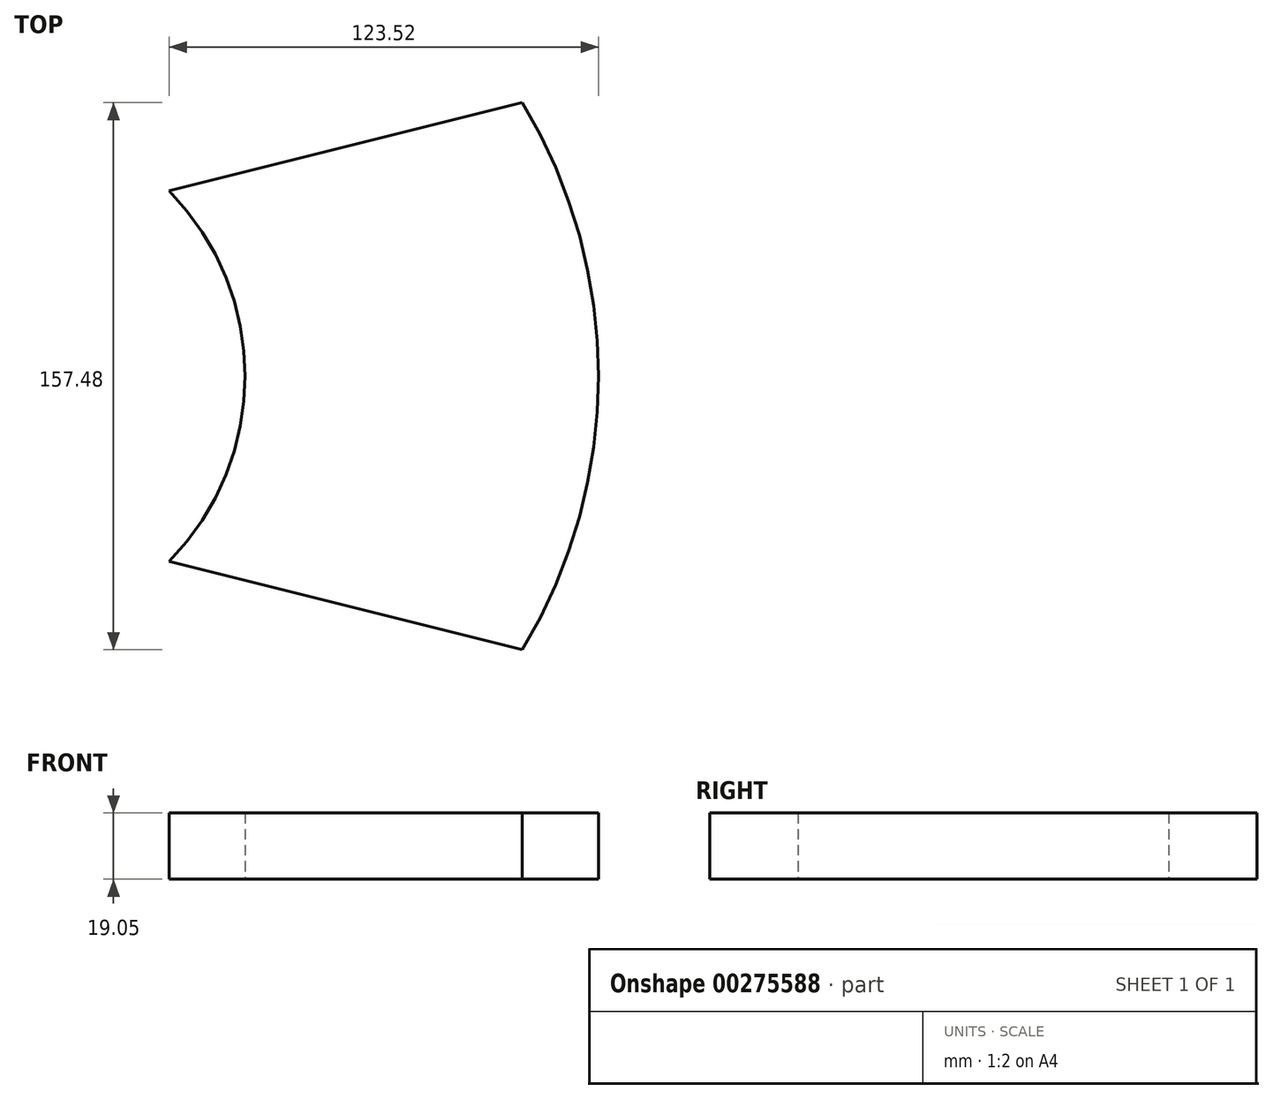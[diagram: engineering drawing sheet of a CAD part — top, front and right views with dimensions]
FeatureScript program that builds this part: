
annotation { "Feature Type Name" : "Feature", "Feature Type Description" : "" }
export const myFeature = defineFeature(function(context is Context, id is Id, definition is map)
    precondition{}
    {
        {
            var Q0;
            Q0=qCreatedBy(makeId("Top.planeOp"),FACE);
            var sketch = newSketch(context, id + "F0", { "sketchPlane" : qUnion([Q0])});
            skLineSegment(sketch, "E0", {"start": v(4.84, 0) * mm, "end": v(-47.06, 0) * mm});
            skLineSegment(sketch, "E1", {"start": v(-47.06, 0) * mm, "end": v(54.54, 0) * mm});
            skLineSegment(sketch, "E2", {"start": v(-47.06, 0) * mm, "end": v(-47.06, 81.28) * mm});
            skLineSegment(sketch, "E3", {"start": v(54.54, 0) * mm, "end": v(54.54, 106.68) * mm});
            skLineSegment(sketch, "E4", {"start": v(54.54, -50.8) * mm, "end": v(54.54, 0) * mm});
            skArc(sketch, "E5", {"start": v(54.54, -50.8) * mm, "mid": v(76.46, 27.94) * mm, "end": v(54.54, 106.68) * mm});
            skLineSegment(sketch, "E6", {"start": v(-47.06, 81.28) * mm, "end": v(54.54, 106.68) * mm});
            skLineSegment(sketch, "E7", {"start": v(-47.06, 0) * mm, "end": v(54.54, -50.8) * mm});
            skLineSegment(sketch, "E8", {"start": v(-47.06, 0) * mm, "end": v(-47.06, -25.4) * mm});
            skLineSegment(sketch, "E9", {"start": v(-47.06, -25.4) * mm, "end": v(54.54, -50.8) * mm});
            skArc(sketch, "E10", {"start": v(-47.06, -25.4) * mm, "mid": v(-25.28, 27.94) * mm, "end": v(-47.06, 81.28) * mm});
            skSolve(sketch);
        }
        {
            var Q0;
            {var subQ4=sQuery(id+"F0.wireOp",EDGE,"E3");Q0=makeQuery(id+"F0.imprint","IMPRINT",FACE,{"disambiguationData":[TD([[makeQuery(id+"F0.imprint","IMPRINT",EDGE,{"derivedFrom":subQ4}),1.0]])]});}
            var Q1;
            {var subQ1=sQuery(id+"F0.wireOp",EDGE,"E4");Q1=makeQuery(id+"F0.imprint","IMPRINT",FACE,{"disambiguationData":[TD([[makeQuery(id+"F0.imprint","IMPRINT",EDGE,{"derivedFrom":subQ1}),1.0]])]});}
            var Q2;
            {var subQ0=sQuery(id+"F0.wireOp",EDGE,"E9");Q2=makeQuery(id+"F0.imprint","IMPRINT",FACE,{"disambiguationData":[TD([[makeQuery(id+"F0.imprint","IMPRINT",EDGE,{"derivedFrom":subQ0}),1.0]])]});}
            var Q3;
            Q3=makeQuery(id+"F0.imprint","IMPRINT",FACE,{"disambiguationData":[TD([[makeQuery(id+"F0.imprint","IMPRINT",EDGE,{"derivedFrom":sQuery(id+"F0.wireOp",EDGE,"E3")}),-1.0]])]});
            extrude(context, id + "F1", {"entities" : qUnion([Q0, Q1, Q2, Q3]), "depth" : 19.05 * mm});
        }
    });
